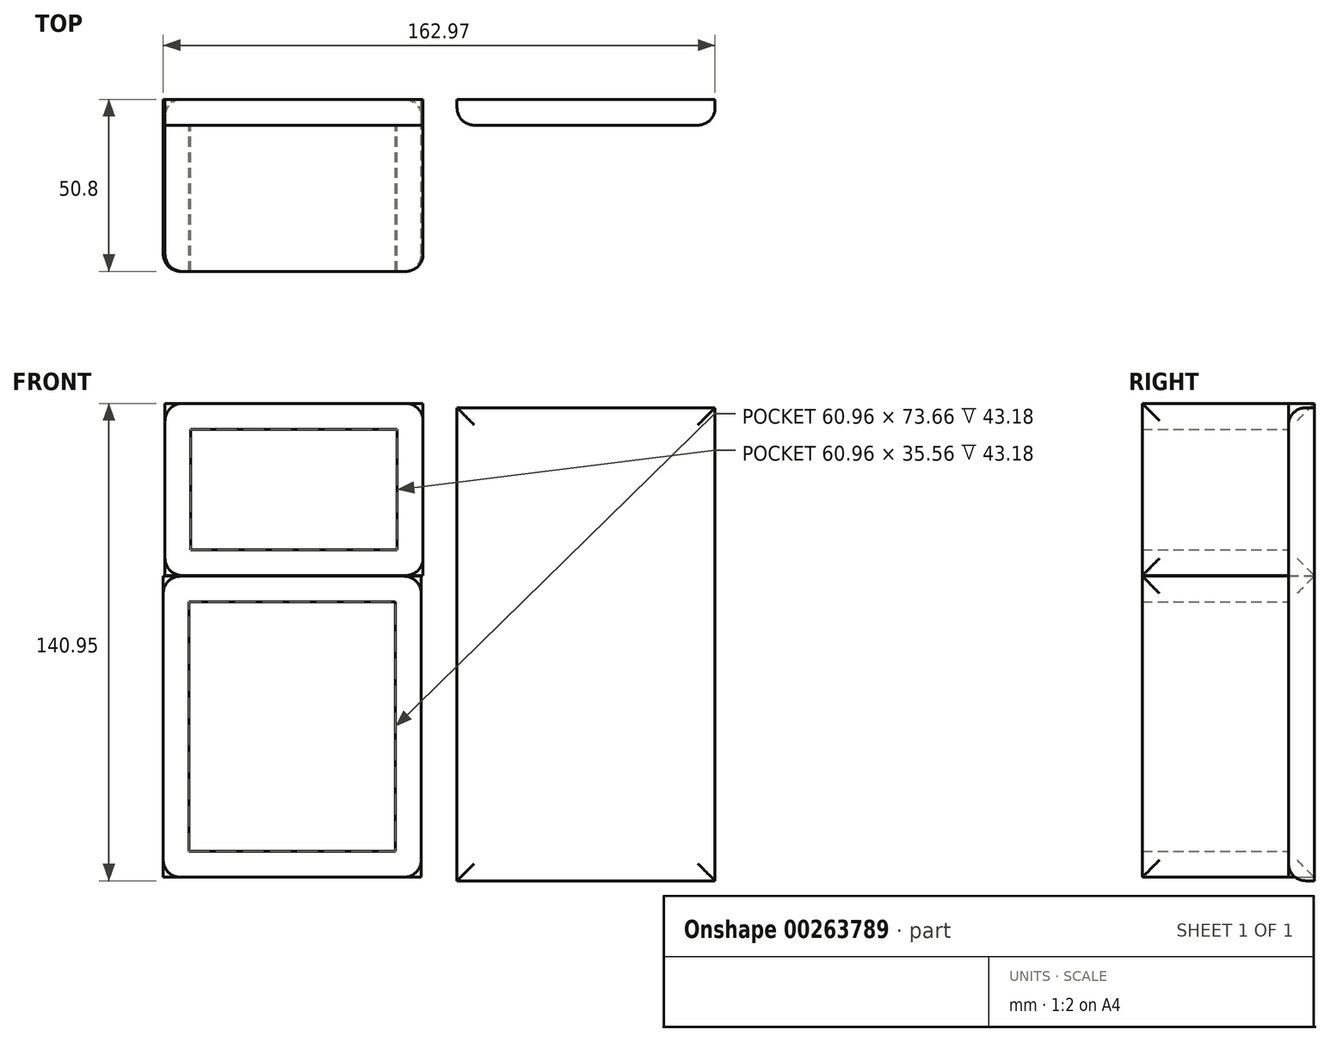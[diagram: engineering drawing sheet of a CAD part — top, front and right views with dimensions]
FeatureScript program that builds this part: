
annotation { "Feature Type Name" : "Feature", "Feature Type Description" : "" }
export const myFeature = defineFeature(function(context is Context, id is Id, definition is map)
    precondition{}
    {
        {
            var Q0;
            Q0=qCreatedBy(makeId("Front.planeOp"),FACE);
            var sketch = newSketch(context, id + "F0", { "sketchPlane" : qUnion([Q0])});
            skLineSegment(sketch, "E0.bottom", {"start": v(-36.2, 76) * mm, "end": v(40, 76) * mm});
            skLineSegment(sketch, "E0.top", {"start": v(-36.2, 25.2) * mm, "end": v(40, 25.2) * mm});
            skLineSegment(sketch, "E0.left", {"start": v(-36.2, 76) * mm, "end": v(-36.2, 25.2) * mm});
            skLineSegment(sketch, "E0.right", {"start": v(40, 76) * mm, "end": v(40, 25.2) * mm});
            skLineSegment(sketch, "E1.bottom", {"start": v(-36.75, 25) * mm, "end": v(39.45, 25) * mm});
            skLineSegment(sketch, "E1.top", {"start": v(-36.75, -63.9) * mm, "end": v(39.45, -63.9) * mm});
            skLineSegment(sketch, "E1.left", {"start": v(-36.75, 25) * mm, "end": v(-36.75, -63.9) * mm});
            skLineSegment(sketch, "E1.right", {"start": v(39.45, 25) * mm, "end": v(39.45, -63.9) * mm});
            skLineSegment(sketch, "E2.bottom", {"start": v(50.02, 74.76) * mm, "end": v(126.22, 74.76) * mm});
            skLineSegment(sketch, "E2.top", {"start": v(50.02, -64.94) * mm, "end": v(126.22, -64.94) * mm});
            skLineSegment(sketch, "E2.left", {"start": v(50.02, 74.76) * mm, "end": v(50.02, -64.94) * mm});
            skLineSegment(sketch, "E2.right", {"start": v(126.22, 74.76) * mm, "end": v(126.22, -64.94) * mm});
            skSolve(sketch);
        }
        {
            var Q0;
            Q0=makeQuery(id+"F0.imprint","IMPRINT",FACE,{"disambiguationData":[TD([[makeQuery(id+"F0.imprint","IMPRINT",EDGE,{"derivedFrom":sQuery(id+"F0.wireOp",EDGE,"E0.bottom")}),-1.0]])]});
            var Q1;
            Q1=makeQuery(id+"F0.imprint","IMPRINT",FACE,{"disambiguationData":[TD([[makeQuery(id+"F0.imprint","IMPRINT",EDGE,{"derivedFrom":sQuery(id+"F0.wireOp",EDGE,"E1.bottom")}),-1.0]])]});
            extrude(context, id + "F1", {"entities" : qUnion([Q0, Q1]), "depth" : 50.8 * mm});
        }
        {
            var Q0;
            Q0=makeQuery(id+"F1.opExtrude","SWEPT_FACE",FACE,{"disambiguationData":[OSD([sQuery(id+"F0.wireOp",EDGE,"E1.left")])]});
            var Q1;
            Q1=makeQuery(id+"F1.opExtrude","SWEPT_FACE",FACE,{"disambiguationData":[OSD([sQuery(id+"F0.wireOp",EDGE,"E1.right")])]});
            var Q2;
            Q2=makeQuery(id+"F1.opExtrude","SWEPT_FACE",FACE,{"disambiguationData":[OSD([sQuery(id+"F0.wireOp",EDGE,"E0.right")])]});
            var Q3;
            Q3=makeQuery(id+"F1.opExtrude","SWEPT_FACE",FACE,{"disambiguationData":[OSD([sQuery(id+"F0.wireOp",EDGE,"E0.left")])]});
            fillet(context, id + "F2", {"entities" : qUnion([Q0, Q1, Q2, Q3]), "radius" : 5.08 * mm, "tangentPropagation" : true, "allowEdgeOverflow" : false});
        }
        {
            var Q0;
            Q0=makeQuery(id+"F1.opExtrude","CAP_FACE",FACE,{"disambiguationData":[OSD([sQuery(id+"F0.wireOp",EDGE,"E1.bottom"),sQuery(id+"F0.wireOp",EDGE,"E1.top"),sQuery(id+"F0.wireOp",EDGE,"E1.left"),sQuery(id+"F0.wireOp",EDGE,"E1.right")])],"isStart":false});
            var Q1;
            Q1=makeQuery(id+"F1.opExtrude","CAP_FACE",FACE,{"disambiguationData":[OSD([sQuery(id+"F0.wireOp",EDGE,"E0.bottom"),sQuery(id+"F0.wireOp",EDGE,"E0.top"),sQuery(id+"F0.wireOp",EDGE,"E0.left"),sQuery(id+"F0.wireOp",EDGE,"E0.right")])],"isStart":false});
            shell(context, id + "F3", {"entities" : qUnion([Q0, Q1]), "thickness" : 7.62 * mm});
        }
        {
            var Q0;
            Q0 = qSketchRegion(id + "F0", true);
            extrude(context, id + "F4", {"entities" : qUnion([Q0]), "depth" : 7.62 * mm});
        }
        {
            var Q0;
            Q0=makeQuery(id+"F4.opExtrude","CAP_FACE",FACE,{"disambiguationData":[OSD([sQuery(id+"F0.wireOp",EDGE,"E2.bottom"),sQuery(id+"F0.wireOp",EDGE,"E2.top"),sQuery(id+"F0.wireOp",EDGE,"E2.left"),sQuery(id+"F0.wireOp",EDGE,"E2.right")])],"isStart":false});
            fillet(context, id + "F5", {"entities" : qUnion([Q0]), "radius" : 5.08 * mm, "tangentPropagation" : true, "allowEdgeOverflow" : false});
        }
    });
